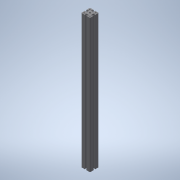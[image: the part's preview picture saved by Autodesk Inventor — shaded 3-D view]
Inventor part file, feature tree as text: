
AUTODESK INVENTOR PART (.ipt)
format: ipt  version: 2022 (Build 260153000, 153)  size: 224,768 bytes
history: native  units: mm (DEFAULTED — no unit token found)
features: other x21, sketch x2, extrude x1, hole x1
ambient origin geometry x8: Origin, YZ Plane, XZ Plane, XY Plane, X Axis, Y Axis, Z Axis, Center Point
bodies: Solid1 (feature_tree)
feature tree (25):
  extrude  "Extrusion1"  TaperAngle=0.0deg  [1 undecoded]
  hole  "Hole1"  [1 undecoded]
  other  "C1_XY"
  other  "C1_YZ"
  other  "C1_ZX"
  other  "C1_X"
  other  "C1_Y"
  other  "C1_Z"
  other  "C1_Center"
  other  "to_frame_cap1_XY"
  other  "to_frame_cap1_YZ"
  other  "to_frame_cap1_ZX"
  other  "to_frame_cap1_X"
  other  "to_frame_cap1_Y"
  other  "to_frame_cap1_Z"
  other  "to_frame_cap1_Center"
  other  "to_frame_cap2_XY"
  other  "to_frame_cap2_YZ"
  other  "to_frame_cap2_ZX"
  other  "to_frame_cap2_X"
  other  "to_frame_cap2_Y"
  other  "to_frame_cap2_Z"
  other  "to_frame_cap2_Center"
  sketch  "Sketch_60"  dims[d2=10.5mm d3=6.0mm d4=4.0mm d5=2.0mm d6=90.0deg d7=1000.0mm d8=0.0mm d9=0.0mm d10=0.0mm d11=0.0mm d12=152.4mm d13=0.872665mm d14=152.4mm d15=0.872665mm]
  sketch  "Sketch2"  dims[d0=914.4mm d1=0.0mm]
note: 2 required parameter values undecoded (feature->parameter linkage not recoverable at this tier; creation-order binding heuristic only, values carry confidence <= 0.55)
